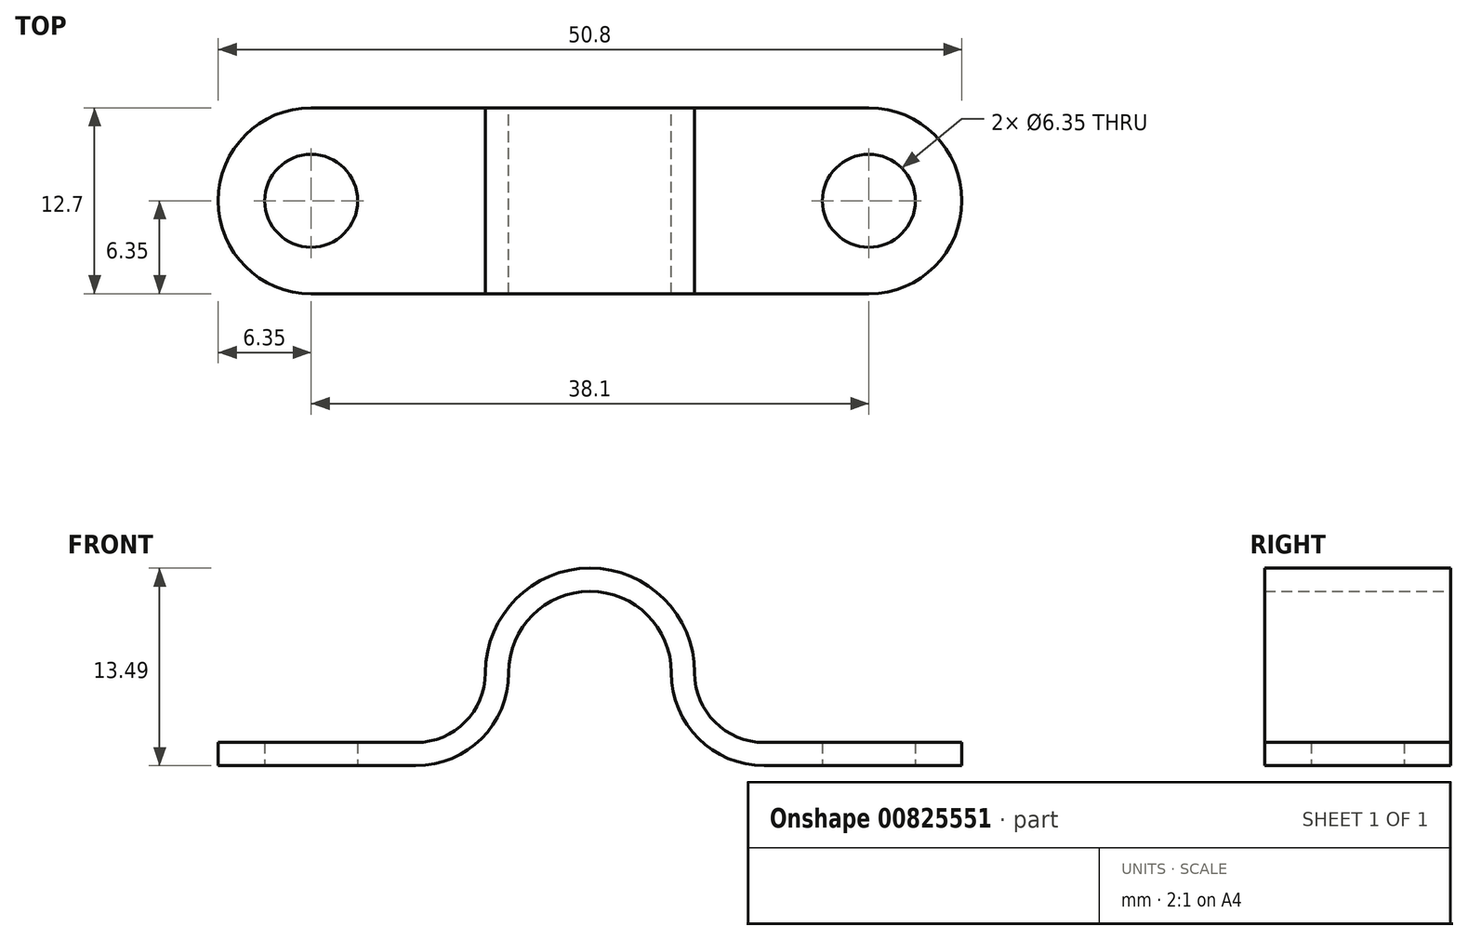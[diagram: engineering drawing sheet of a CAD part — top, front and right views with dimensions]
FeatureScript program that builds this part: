
annotation { "Feature Type Name" : "Feature", "Feature Type Description" : "" }
export const myFeature = defineFeature(function(context is Context, id is Id, definition is map)
    precondition{}
    {
        {
            var Q0;
            Q0=qCreatedBy(makeId("Front.planeOp"),FACE);
            var sketch = newSketch(context, id + "F0", { "sketchPlane" : qUnion([Q0])});
            skLineSegment(sketch, "E0.bottom", {"start": v(-25.4, 0.8) * mm, "end": v(-11.9, 0.8) * mm});
            skLineSegment(sketch, "E0.top", {"start": v(-25.4, -0.8) * mm, "end": v(-11.9, -0.8) * mm});
            skLineSegment(sketch, "E0.left", {"start": v(-25.4, 0.8) * mm, "end": v(-25.4, -0.8) * mm});
            skLineSegment(sketch, "E0.right", {"start": v(25.4, 0.8) * mm, "end": v(25.4, -0.8) * mm});
            skPoint(sketch, "E0.middle", {"position": v(0, 0) * mm});
            skLineSegment(sketch, "E1", {"start": v(-7.14, 5.56) * mm, "end": v(-7.14, 5.56) * mm});
            skLineSegment(sketch, "E2", {"start": v(7.14, 5.56) * mm, "end": v(7.14, 5.56) * mm});
            skArc(sketch, "E3.trimOffspring", {"start": v(5.56, 5.56) * mm, "mid": v(0, 11.11) * mm, "end": v(-5.56, 5.56) * mm});
            skArc(sketch, "E4.trimOffspring", {"start": v(7.14, 5.56) * mm, "mid": v(0, 12.7) * mm, "end": v(-7.14, 5.56) * mm});
            skLineSegment(sketch, "E5.trimOffspring", {"start": v(11.9, 0.8) * mm, "end": v(25.4, 0.8) * mm});
            skLineSegment(sketch, "E6.trimOffspring", {"start": v(11.9, -0.8) * mm, "end": v(25.4, -0.8) * mm});
            skPoint(sketch, "E7.visualSharp", {"position": v(-7.14, 0.8) * mm});
            skArc(sketch, "E7.filletArc", {"start": v(-11.9, 0.8) * mm, "mid": v(-8.54, 2.19) * mm, "end": v(-7.14, 5.56) * mm});
            skPoint(sketch, "E8.visualSharp", {"position": v(7.14, 0.8) * mm});
            skArc(sketch, "E8.filletArc", {"start": v(7.14, 5.56) * mm, "mid": v(8.54, 2.19) * mm, "end": v(11.9, 0.8) * mm});
            skArc(sketch, "E9.0", {"start": v(-11.9, -0.8) * mm, "mid": v(-7.42, 1.07) * mm, "end": v(-5.56, 5.56) * mm});
            skArc(sketch, "E10.0", {"start": v(5.56, 5.56) * mm, "mid": v(7.42, 1.07) * mm, "end": v(11.9, -0.8) * mm});
            skSolve(sketch);
        }
        {
            var Q0;
            Q0=makeQuery(id+"F0.imprint","IMPRINT",FACE,{"disambiguationData":[TD([[makeQuery(id+"F0.imprint","IMPRINT",EDGE,{"derivedFrom":sQuery(id+"F0.wireOp",EDGE,"E0.bottom")}),-1.0]])]});
            extrude(context, id + "F1", {"entities" : qUnion([Q0]), "endBound" : BoundingType.SYMMETRIC, "depth" : 12.7 * mm, "offsetDistance" : 25.4 * mm});
        }
        {
            var Q0;
            Q0=makeQuery(id+"F1.opExtrude","CAP_EDGE",EDGE,{"disambiguationData":[OSD([sQuery(id+"F0.wireOp",EDGE,"E0.right")])],"isStart":false});
            var Q1;
            Q1=makeQuery(id+"F1.opExtrude","CAP_EDGE",EDGE,{"disambiguationData":[OSD([sQuery(id+"F0.wireOp",EDGE,"E0.right")])],"isStart":true});
            var Q2;
            Q2=makeQuery(id+"F1.opExtrude","CAP_EDGE",EDGE,{"disambiguationData":[OSD([sQuery(id+"F0.wireOp",EDGE,"E0.left")])],"isStart":false});
            var Q3;
            Q3=makeQuery(id+"F1.opExtrude","CAP_EDGE",EDGE,{"disambiguationData":[OSD([sQuery(id+"F0.wireOp",EDGE,"E0.left")])],"isStart":true});
            fillet(context, id + "F2", {"entities" : qUnion([Q0, Q1, Q2, Q3]), "radius" : 6.35 * mm, "tangentPropagation" : true, "allowEdgeOverflow" : false});
        }
        {
            var Q0;
            Q0=qCreatedBy(makeId("Top.planeOp"),FACE);
            var sketch = newSketch(context, id + "F3", { "sketchPlane" : qUnion([Q0])});
            skCircle(sketch, "E11", {"center": v(-19.05, 0) * mm, "radius": 3.18 * mm});
            skCircle(sketch, "E12", {"center": v(19.05, 0) * mm, "radius": 3.18 * mm});
            skSolve(sketch);
        }
        {
            var Q0;
            Q0=sQuery(id+"F3.wireOp",VERTEX,"E11.center");
            var Q1;
            Q1=sQuery(id+"F3.wireOp",VERTEX,"E12.center");
            var Q2;
            Q2=makeQuery(id+"F1.opExtrude","SWEPT_BODY",BODY,{"disambiguationData":[OSD([sQuery(id+"F0.wireOp",EDGE,"E0.bottom"),sQuery(id+"F0.wireOp",EDGE,"E0.top"),sQuery(id+"F0.wireOp",EDGE,"E0.left"),sQuery(id+"F0.wireOp",EDGE,"E0.right"),sQuery(id+"F0.wireOp",EDGE,"E3.trimOffspring"),sQuery(id+"F0.wireOp",EDGE,"E4.trimOffspring"),sQuery(id+"F0.wireOp",EDGE,"E5.trimOffspring"),sQuery(id+"F0.wireOp",EDGE,"E6.trimOffspring"),sQuery(id+"F0.wireOp",EDGE,"E7.filletArc"),sQuery(id+"F0.wireOp",EDGE,"E8.filletArc"),sQuery(id+"F0.wireOp",EDGE,"E9.0"),sQuery(id+"F0.wireOp",EDGE,"E10.0")])]});
            hole(context, id + "F4", {"style" : HoleStyle.SIMPLE, "endStyle" : HoleEndStyle.THROUGH, "oppositeDirection" : true, "holeDiameter" : 6.35 * mm, "majorDiameter" : 6.35 * mm, "isTappedThrough" : true, "tappedDepth" : 12.7 * mm, "tapClearance" : 3, "locations" : qUnion([Q0, Q1]), "scope" : qUnion([Q2])});
        }
        {
            var Q0;
            Q0=sQuery(id+"F3.wireOp",VERTEX,"E11.center");
            var Q1;
            Q1=sQuery(id+"F3.wireOp",VERTEX,"E12.center");
            var Q2;
            Q2=makeQuery(id+"F1.opExtrude","SWEPT_BODY",BODY,{"disambiguationData":[OSD([sQuery(id+"F0.wireOp",EDGE,"E0.bottom"),sQuery(id+"F0.wireOp",EDGE,"E0.top"),sQuery(id+"F0.wireOp",EDGE,"E0.left"),sQuery(id+"F0.wireOp",EDGE,"E0.right"),sQuery(id+"F0.wireOp",EDGE,"E3.trimOffspring"),sQuery(id+"F0.wireOp",EDGE,"E4.trimOffspring"),sQuery(id+"F0.wireOp",EDGE,"E5.trimOffspring"),sQuery(id+"F0.wireOp",EDGE,"E6.trimOffspring"),sQuery(id+"F0.wireOp",EDGE,"E7.filletArc"),sQuery(id+"F0.wireOp",EDGE,"E8.filletArc"),sQuery(id+"F0.wireOp",EDGE,"E9.0"),sQuery(id+"F0.wireOp",EDGE,"E10.0")])]});
            hole(context, id + "F5", {"style" : HoleStyle.SIMPLE, "endStyle" : HoleEndStyle.THROUGH, "holeDiameter" : 6.35 * mm, "majorDiameter" : 6.35 * mm, "isTappedThrough" : true, "tappedDepth" : 12.7 * mm, "tapClearance" : 3, "locations" : qUnion([Q0, Q1]), "scope" : qUnion([Q2])});
        }
    });
